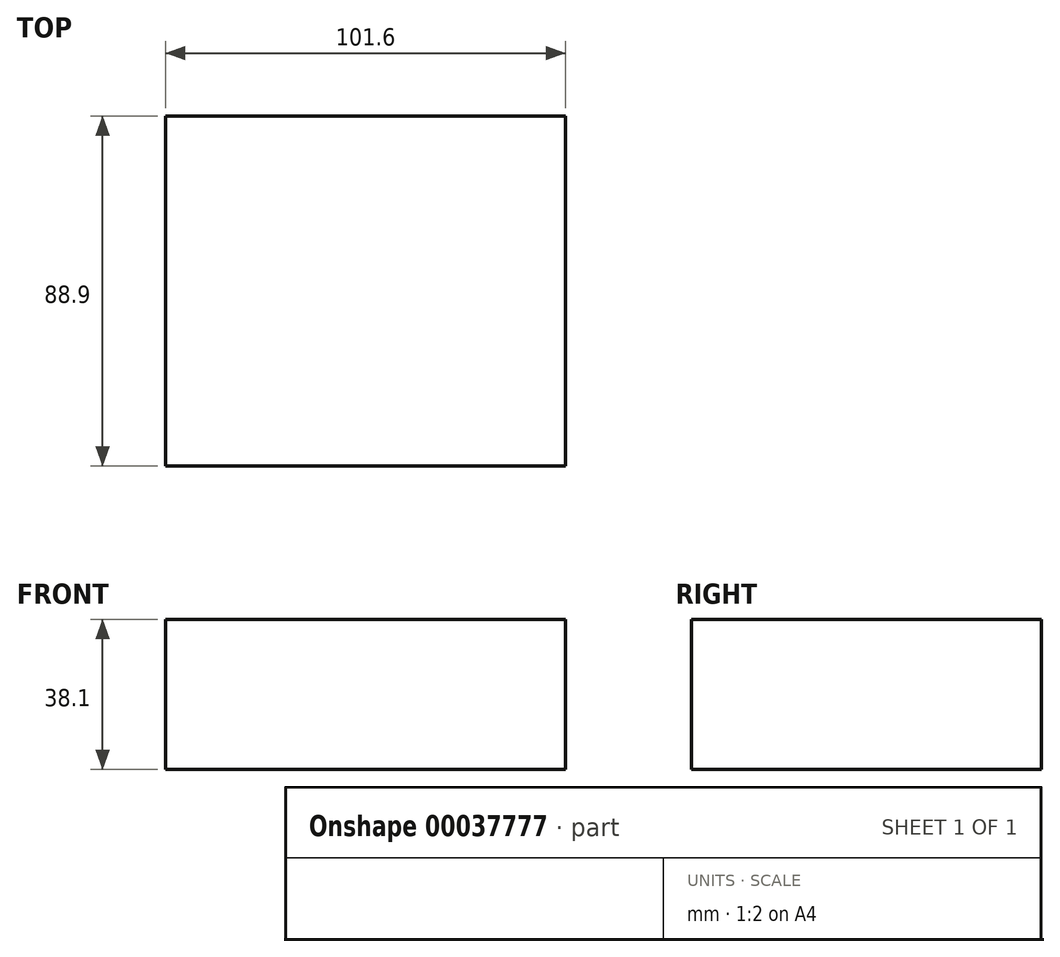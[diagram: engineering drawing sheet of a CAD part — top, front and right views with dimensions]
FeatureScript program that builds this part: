
annotation { "Feature Type Name" : "Feature", "Feature Type Description" : "" }
export const myFeature = defineFeature(function(context is Context, id is Id, definition is map)
    precondition{}
    {
        {
            var Q0;
            Q0=qCreatedBy(makeId("Top.planeOp"),FACE);
            var sketch = newSketch(context, id + "F0", { "sketchPlane" : qUnion([Q0])});
            skLineSegment(sketch, "E0.bottom", {"start": v(0, 0) * mm, "end": v(101.6, 0) * mm});
            skLineSegment(sketch, "E0.top", {"start": v(0, -88.9) * mm, "end": v(101.6, -88.9) * mm});
            skLineSegment(sketch, "E0.left", {"start": v(0, 0) * mm, "end": v(0, -88.9) * mm});
            skLineSegment(sketch, "E0.right", {"start": v(101.6, 0) * mm, "end": v(101.6, -88.9) * mm});
            skSolve(sketch);
        }
        {
            var Q0;
            Q0 = qSketchRegion(id + "F0", true);
            extrude(context, id + "F1", {"entities" : qUnion([Q0]), "depth" : 38.1 * mm});
        }
    });
